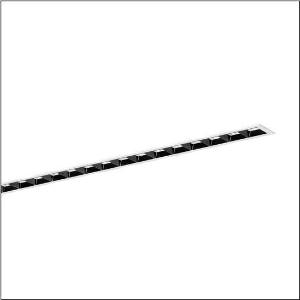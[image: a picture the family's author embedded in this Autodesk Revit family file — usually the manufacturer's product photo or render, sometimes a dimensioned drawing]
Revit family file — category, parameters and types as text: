
# Revit family: silica_r__21_51mx14da34wb_b271
name_source: partatom
category: Lighting Fixtures
units: mm (PartAtom-declared; Revit-internal decimal feet)

## family parameters
Cut with Voids When Loaded = No
Host = Face
Light Source = No
Part Type = Normal
Room Calculation Point = No
Round Connector Dimension = Use Diameter
Shared = No

## types (1)
- --- (1 x LED, 4320 lm, 32.1 W, 3000K)
    Apparent Load = 32 VA
    CIE Flux Codes = 74 94 99 100 100
    Color Rendering = 80
    Color Temperature = 3000K
    Default Elevation = 1800 mm
    Description = Silica® 21, office luminaire, primary light control with darklight reflector, of PMMA, black, light emission: direct distribution, primary light characteristic: asymmetric, installation type: recessed, LED, rated luminous flux: 4.320lm, luminous efficacy: 135lm/W, light colour: 830, colour temperature: 3000K, with terminal, 3+2-pole, max. 2.5mm², mains connection: 220..240V, AC, 50/60Hz, rated input power: 32.1W, luminaire housing, of aluminium, traffic white (RAL 9016), length: 1.228mm, width: 79mm, height: 53mm, protection rating (complete): IP20, insulation class (complete): insulation class I (protective earthing), certification: CE, permissible operating ambient temperature: 0..+35°C, standard: EN 50419, packaging unit: 1 piece
    Height = 0 mm  [stored 0 ft]
    Lamp = 1 x LED
    Lamp Light Flux = 4320 lm
    Lamp Power = 32.1 W
    Lamp count = 1
    Length = 1227 mm
    Luminous efficacy = 135 lm/W
    Manufacturer = Siteco
    ModVariant = No
    Model = 51MX14DA34WB
    Mounting Place = Ceiling
    Mounting Type = Recessed
    Number of Poles = 1
    OnlyDefault = Yes
    Power Factor = 1
    Product Name = Silica® 21
    Product group = office luminaire | ceiling recessed
    ProductGroupID = 401
    Protection Class = Protection class I
    Protection Degree = IP 20
    RLX_Detail_Level = 1
    RLX_Emergency_Light_Flux = 0 lm
    RLX_Emergency_Type = 0
    RLX_Emergency_Type_DB = No
    RlxData = <blob elided: 39289 chars, md5=6ba4ac8b>
    Socket = socket
    Standby Power = 0 W
    System Light Flux = 4320 lm
    System Power = 32 W
    Type Comments = factory setting: luminous flux: 100 % | dim-lin: 254 | 448 mA
    Type Image = l_1313610.jpg
    URL = http://relux.com
    VarID = @adj_071341
    Voltage = 0 V
    Weight = 0.00 kg
    Width = 79 mm

note: [stored X ft] marks values corroborated as IEEE doubles in the binary element streams (Revit-internal decimal feet)

## geometry (parser evidence)
native form markers: Blend x4, Sweep x12
no freeform markers — native parametric forms only
